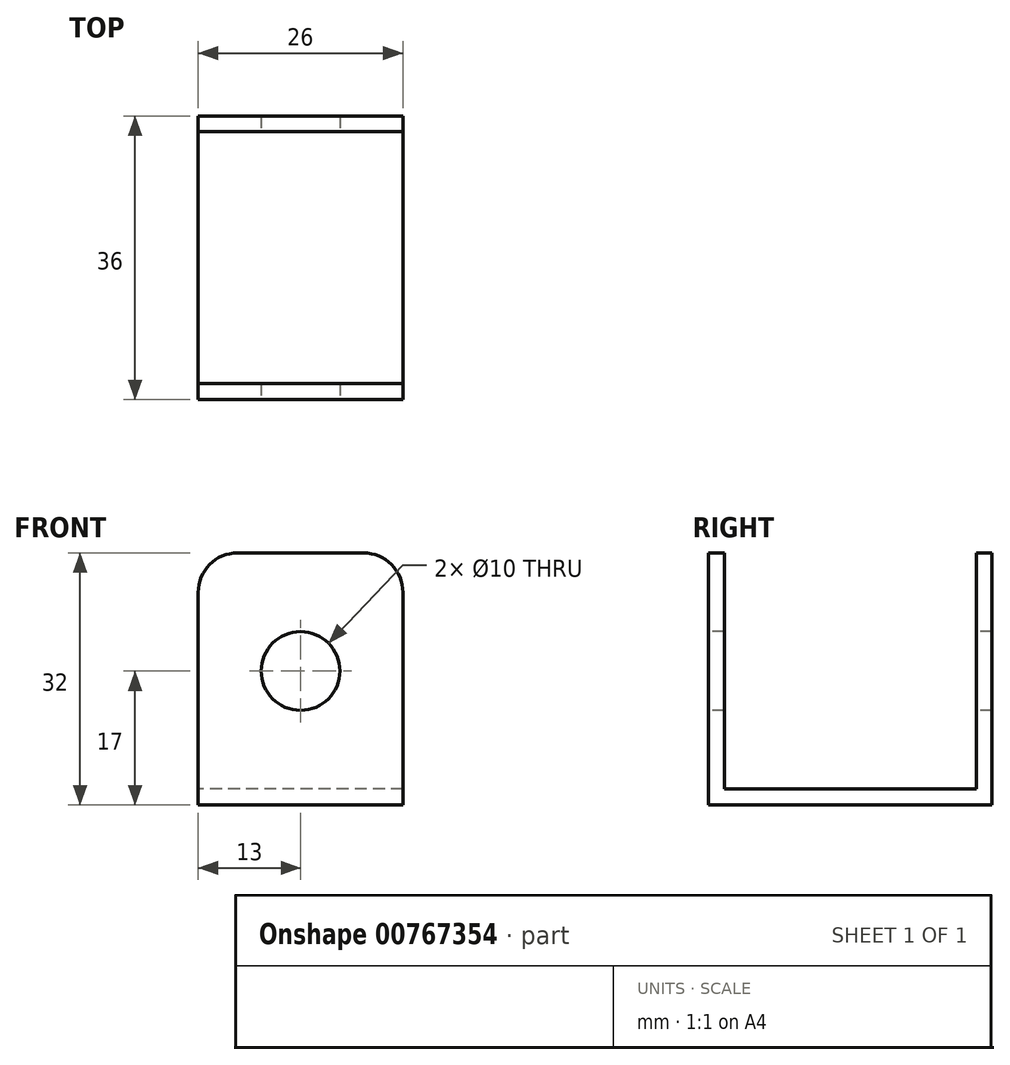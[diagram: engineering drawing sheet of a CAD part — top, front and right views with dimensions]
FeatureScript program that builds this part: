
annotation { "Feature Type Name" : "Feature", "Feature Type Description" : "" }
export const myFeature = defineFeature(function(context is Context, id is Id, definition is map)
    precondition{}
    {
        {
            var Q0;
            Q0=qCreatedBy(makeId("Right.planeOp"),FACE);
            var sketch = newSketch(context, id + "F0", { "sketchPlane" : qUnion([Q0])});
            skLineSegment(sketch, "E0.bottom", {"start": v(-1, 15) * mm, "end": v(1, 15) * mm});
            skLineSegment(sketch, "E0.top", {"start": v(-1, -15) * mm, "end": v(1, -15) * mm});
            skLineSegment(sketch, "E0.left", {"start": v(-1, 15) * mm, "end": v(-1, -15) * mm});
            skLineSegment(sketch, "E0.right", {"start": v(1, 15) * mm, "end": v(1, -15) * mm});
            skPoint(sketch, "E0.middle", {"position": v(0, 0) * mm});
            skLineSegment(sketch, "E1.bottom", {"start": v(-1, -15) * mm, "end": v(35, -15) * mm});
            skLineSegment(sketch, "E1.top", {"start": v(-1, -17) * mm, "end": v(35, -17) * mm});
            skLineSegment(sketch, "E1.left", {"start": v(-1, -15) * mm, "end": v(-1, -17) * mm});
            skLineSegment(sketch, "E1.right", {"start": v(35, -15) * mm, "end": v(35, -17) * mm});
            skLineSegment(sketch, "E2.bottom", {"start": v(35, -15) * mm, "end": v(33, -15) * mm});
            skLineSegment(sketch, "E2.top", {"start": v(35, 15) * mm, "end": v(33, 15) * mm});
            skLineSegment(sketch, "E2.left", {"start": v(35, -15) * mm, "end": v(35, 15) * mm});
            skLineSegment(sketch, "E2.right", {"start": v(33, -15) * mm, "end": v(33, 15) * mm});
            skSolve(sketch);
        }
        {
            var Q0;
            Q0 = qSketchRegion(id + "F0", true);
            extrude(context, id + "F1", {"entities" : qUnion([Q0]), "depth" : 26 * mm, "offsetDistance" : 25 * mm});
        }
        {
            var Q0;
            Q0=qCreatedBy(makeId("Front.planeOp"),FACE);
            var sketch = newSketch(context, id + "F2", { "sketchPlane" : qUnion([Q0])});
            skCircle(sketch, "E3", {"center": v(13, 0) * mm, "radius": 5 * mm});
            skSolve(sketch);
        }
        {
            var Q0;
            Q0 = qSketchRegion(id + "F2", true);
            extrude(context, id + "F3", {"entities" : qUnion([Q0]), "operationType" : NewBodyOperationType.REMOVE, "oppositeDirection" : true, "depth" : 40.2 * mm, "offsetDistance" : 25 * mm});
        }
        {
            var Q0;
            Q0=qCreatedBy(makeId("Front.planeOp"),FACE);
            var sketch = newSketch(context, id + "F4", { "sketchPlane" : qUnion([Q0])});
            skCircle(sketch, "E4", {"center": v(13, 0) * mm, "radius": 5 * mm});
            skSolve(sketch);
        }
        {
            var Q0;
            Q0 = qSketchRegion(id + "F4", true);
            extrude(context, id + "F5", {"entities" : qUnion([Q0]), "operationType" : NewBodyOperationType.REMOVE, "depth" : 23 * mm, "offsetDistance" : 25 * mm});
        }
        {
            var Q0;
            Q0=makeQuery(id+"F1.opExtrude","CAP_EDGE",EDGE,{"disambiguationData":[OSD([sQuery(id+"F0.wireOp",EDGE,"E0.bottom")])],"isStart":false});
            var Q1;
            Q1=makeQuery(id+"F1.opExtrude","CAP_EDGE",EDGE,{"disambiguationData":[OSD([sQuery(id+"F0.wireOp",EDGE,"E2.top")])],"isStart":false});
            var Q2;
            Q2=makeQuery(id+"F1.opExtrude","CAP_EDGE",EDGE,{"disambiguationData":[OSD([sQuery(id+"F0.wireOp",EDGE,"E0.bottom")])],"isStart":true});
            var Q3;
            Q3=makeQuery(id+"F1.opExtrude","CAP_EDGE",EDGE,{"disambiguationData":[OSD([sQuery(id+"F0.wireOp",EDGE,"E2.top")])],"isStart":true});
            fillet(context, id + "F6", {"entities" : qUnion([Q0, Q1, Q2, Q3]), "radius" : 5 * mm, "tangentPropagation" : true, "allowEdgeOverflow" : false});
        }
    });
